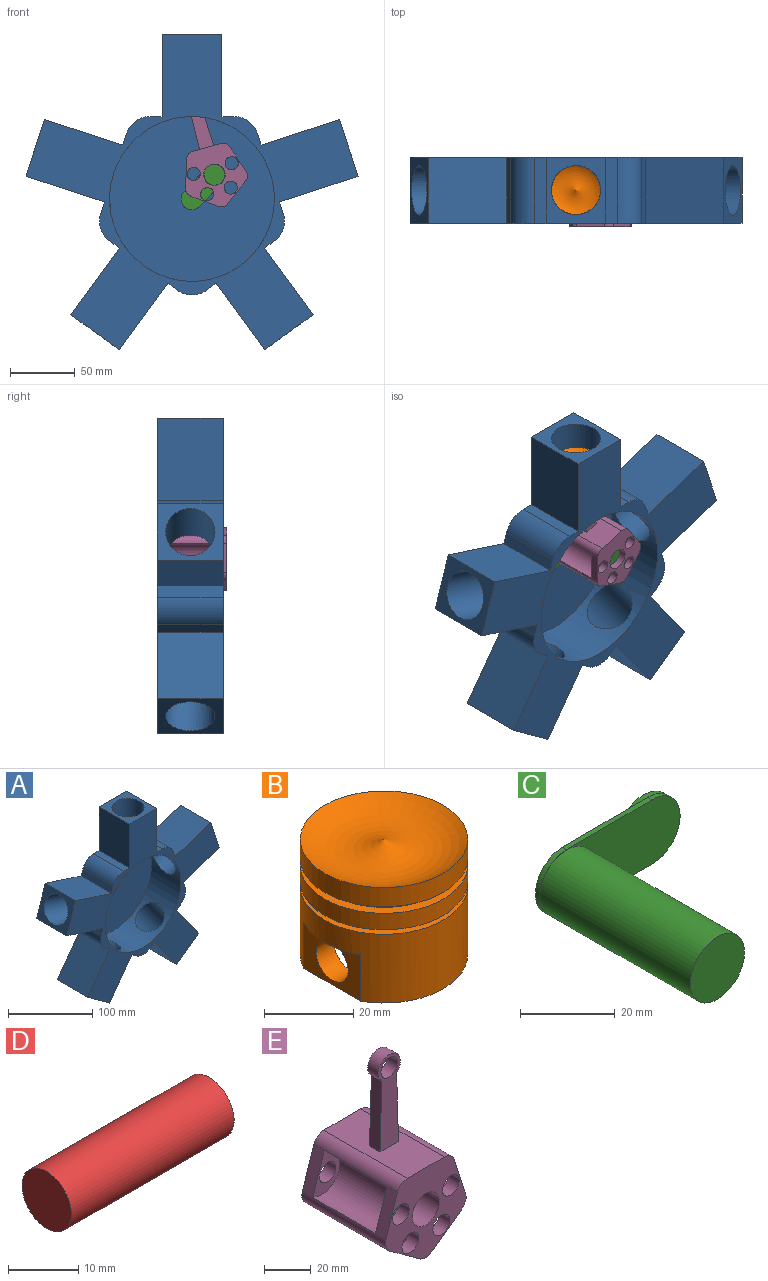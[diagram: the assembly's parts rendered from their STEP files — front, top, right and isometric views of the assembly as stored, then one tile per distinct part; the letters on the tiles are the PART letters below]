
ASSEMBLY  parts=5 mates=6
PART A: 40 faces, bbox 255.8x50.8x243.3 mm
  f0: plane 50.8x7.46mm, normal (0.59,0,-0.81), area 468.5mm2, adj f1,f25,f26,f39
  f1: plane 51.37x50.8mm, normal (-0.81,0,-0.59), area 3225.8mm2, adj f0,f2,f25,f26
  f2: plane 50.8x37.32mm, normal (0.59,0,-0.81), area 1203.1mm2, adj f1,f3,f25,f26,f34
  f3: plane 51.38x50.8mm, normal (0.81,0,0.59), area 3225.8mm2, adj f2,f4,f25,f26
  f4: plane 50.8x7.46mm, normal (0.59,0,-0.81), area 468.5mm2, adj f3,f25,f26,f35
  f5: plane 50.8x8.77mm, normal (0.95,0,0.31), area 468.5mm2, adj f6,f25,f26,f35
  f6: plane 60.39x50.8mm, normal (0.31,0,-0.95), area 3225.8mm2, adj f5,f7,f25,f26
  f7: plane 50.8x43.88mm, normal (0.95,0,0.31), area 1203.7mm2, adj f6,f8,f25,f26,f33
  f8: plane 60.39x50.8mm, normal (-0.31,0,0.95), area 3225.8mm2, adj f7,f9,f25,f26
  f9: plane 50.8x8.78mm, normal (0.95,0,0.31), area 468.8mm2, adj f8,f25,f26,f36
  f10: plane 50.8x9.22mm, normal (0,0,1), area 468.5mm2, adj f11,f25,f26,f36
  f11: plane 63.5x50.8mm, normal (1,0,0), area 3225.8mm2, adj f10,f12,f25,f26
  f12: plane 50.8x46.14mm, normal (0,0,1), area 1204mm2, adj f11,f13,f25,f26,f32
  f13: plane 63.5x50.8mm, normal (-1,0,0), area 3225.8mm2, adj f12,f14,f25,f26
  f14: plane 50.8x9.22mm, normal (0,0,1), area 468.5mm2, adj f13,f25,f26,f37
  f15: plane 50.8x8.77mm, normal (-0.95,0,0.31), area 468.5mm2, adj f16,f25,f26,f37
  f16: plane 60.39x50.8mm, normal (0.31,0,0.95), area 3225.8mm2, adj f15,f17,f25,f26
  f17: plane 50.8x43.87mm, normal (-0.95,0,0.31), area 1203.1mm2, adj f16,f18,f25,f26,f31
  f18: plane 60.39x50.8mm, normal (-0.31,0,-0.95), area 3225.8mm2, adj f17,f19,f25,f26
  f19: plane 50.8x8.77mm, normal (-0.95,0,0.31), area 468.5mm2, adj f18,f25,f26,f38
  f20: plane 50.8x7.46mm, normal (-0.59,0,-0.81), area 468.5mm2, adj f21,f25,f26,f38
  f21: plane 51.37x50.8mm, normal (-0.81,0,0.59), area 3225.8mm2, adj f20,f22,f25,f26
  f22: plane 50.8x37.33mm, normal (-0.59,0,-0.81), area 1204mm2, adj f21,f23,f25,f26,f30
  f23: plane 51.37x50.8mm, normal (0.81,0,-0.59), area 3225.8mm2, adj f22,f24,f25,f26
  f24: plane 50.8x7.46mm, normal (-0.59,0,-0.81), area 468.5mm2, adj f23,f25,f26,f39
  f25: plane 255.82x243.31mm, normal (0,-1,0), area 16451.4mm2, adj f0,f1,f2,f3,f4,f5,f6,f7
  f26: plane 255.82x243.31mm, normal (0,1,0), area 28901.7mm2, adj f0,f1,f2,f3,f4,f5,f6,f7
  f27: cylinder r=63.5mm len=127mm, axis (0,-1,0), area 13980.7mm2, adj f25,f28,f30,f31,f32,f33,f34
  f28: plane 127x127mm, normal (0,-1,0), area 12450.3mm2, adj f27,f29
  f29: cylinder r=8.32mm len=16.64mm, axis (0,1,0), area 66.4mm2, adj f26,f28
  f30: cylinder r=19.05mm len=76.13mm, axis (-0.59,0,-0.81), area 7774.4mm2, adj f22,f27
  f31: cylinder r=19.05mm len=74.95mm, axis (-0.95,0,0.31), area 7774.4mm2, adj f17,f27
  f32: cylinder r=19.05mm len=66.43mm, axis (0,0,1), area 7774.4mm2, adj f12,f27
  f33: cylinder r=19.05mm len=74.95mm, axis (0.95,0,0.31), area 7774.4mm2, adj f7,f27
  f34: cylinder r=19.05mm len=76.13mm, axis (0.59,0,-0.81), area 7774.4mm2, adj f2,f27
  f35: cylinder r=19.05mm len=50.8mm, axis (0,1,0), area 1216.1mm2, adj f4,f5,f25,f26
  f36: cylinder r=19.05mm len=50.8mm, axis (0,1,0), area 1216.1mm2, adj f9,f10,f25,f26
  f37: cylinder r=19.05mm len=50.8mm, axis (0,1,0), area 1216.1mm2, adj f14,f15,f25,f26
  f38: cylinder r=19.05mm len=50.8mm, axis (0,1,0), area 1216.1mm2, adj f19,f20,f25,f26
  f39: cylinder r=19.05mm len=50.8mm, axis (0,1,0), area 1216.1mm2, adj f0,f24,f25,f26
PART B: 22 faces, bbox 37.6x37.6x31.8 mm
  f0: plane 37.59x32.66mm, normal (0,0,-1), area 407.5mm2, adj f9,f13,f14,f15,f16,f17,f18
  f1: plane 18.1x2.32mm, normal (0,0,-1), area 28.4mm2, adj f9,f14
  f2: cylinder r=18.8mm len=37.59mm, axis (0,0,-1), area 532.7mm2, adj f3,f12
  f3: plane 37.59x37.59mm, normal (0,0,1), area 256.8mm2, adj f2,f4
  f4: cylinder r=16.48mm len=32.96mm, axis (0,0,-1), area 189.7mm2, adj f3,f5
  f5: plane 37.59x37.59mm, normal (0,0,-1), area 256.8mm2, adj f4,f6
  f6: cylinder r=18.8mm len=37.59mm, axis (0,0,-1), area 620mm2, adj f5,f7
  f7: torus R=9.4mm, axis (0,0,-1), area 1174.3mm2, adj f6
  f8: plane 19.13x2.62mm, normal (0,0,-1), area 33.8mm2, adj f9,f13
  f9: cylinder r=18.8mm len=37.59mm, axis (0,0,-1), area 1736mm2, adj f0,f1,f8,f10,f13,f14
  f10: plane 37.59x37.59mm, normal (0,0,1), area 409.8mm2, adj f9,f11
  f11: cylinder r=14.93mm len=29.86mm, axis (0,0,-1), area 119mm2, adj f10,f12
  f12: plane 37.59x37.59mm, normal (0,0,-1), area 409.8mm2, adj f2,f11
  f13: plane 19.13x12.7mm, normal (1,0,0), area 161.9mm2, adj f0,f8,f9,f21
  f14: plane 18.1x12.7mm, normal (-1,0,0), area 148.7mm2, adj f0,f1,f9,f20
  f15: plane 22.8x17.78mm, normal (-1,0,0), area 324.3mm2, adj f0,f16,f18,f19,f21
  f16: cylinder r=14.68mm len=21.6mm, axis (0,0,-1), area 431.6mm2, adj f0,f15,f17,f19
  f17: plane 22.8x17.78mm, normal (1,0,0), area 324.3mm2, adj f0,f16,f18,f19,f20
  f18: cylinder r=13.96mm len=21.6mm, axis (0,0,-1), area 439.2mm2, adj f0,f15,f17,f19
  f19: plane 32.66x21.6mm, normal (0,0,-1), area 640.2mm2, adj f15,f16,f17,f18
  f20: cylinder r=5.08mm len=10.16mm, axis (1,0,0), area 179.7mm2, adj f14,f17
  f21: cylinder r=5.08mm len=10.16mm, axis (1,0,0), area 173.1mm2, adj f13,f15
PART C: 12 faces, bbox 41.9x47.5x16.6 mm
  f0: cylinder r=8.31mm len=16.61mm, axis (0,1,0), area 66.3mm2, adj f1,f2,f5,f8
  f1: plane 16.61x16.61mm, normal (0,1,0), area 216.7mm2, adj f0
  f2: plane 33.47x16.61mm, normal (0,1,0), area 412.8mm2, adj f0,f3,f5,f6
  f3: plane 25.4x1.27mm, normal (-0.01,0,-1), area 32.3mm2, adj f2,f4,f6,f7,f8
  f4: cylinder r=8.31mm len=16.61mm, axis (0,1,0), area 33.3mm2, adj f3,f5,f7,f8
  f5: plane 25.46x1.27mm, normal (-0.01,0,1), area 32.3mm2, adj f0,f2,f4,f6,f7
  f6: cylinder r=8.13mm len=16.26mm, axis (0,1,0), area 32.4mm2, adj f2,f3,f5,f7,f9
  f7: plane 39.82x16.61mm, normal (0,-1,0), area 425.3mm2, adj f3,f4,f5,f6,f10
  f8: plane 16.61x8.42mm, normal (0,1,0), area 1mm2, adj f0,f3,f4
  f9: plane 10.84x2.09mm, normal (0,1,0), area 0.1mm2, adj f6,f10
  f10: cylinder r=8.09mm len=44.96mm, axis (0,1,0), area 2284.1mm2, adj f7,f9,f11
  f11: plane 16.17x16.17mm, normal (0,-1,0), area 205.4mm2, adj f10
PART D: 3 faces, bbox 32.7x9.9x9.9 mm
  f0: cylinder r=4.95mm len=32.66mm, axis (-1,0,0), area 1016.5mm2, adj f1,f2
  f1: plane 9.91x9.91mm, normal (1,0,0), area 77.1mm2, adj f0
  f2: plane 9.91x9.91mm, normal (-1,0,0), area 77.1mm2, adj f0
PART E: 43 faces, bbox 49.1x50.8x95.7 mm
  f0: plane 48.46x13.55mm, normal (0,-1,0), area 422.5mm2, adj f11,f25,f26,f27,f28
  f1: plane 21.51x19.42mm, normal (0,-1,0), area 162.5mm2, adj f5,f18,f21
  f2: plane 22.6x16.5mm, normal (0,-1,0), area 161.6mm2, adj f13,f15,f24
  f3: plane 22.61x16.54mm, normal (0,-1,0), area 162.6mm2, adj f9,f16,f23
  f4: plane 21.51x19.42mm, normal (0,-1,0), area 162.6mm2, adj f7,f17,f22
  f5: plane 18.18x13.21mm, normal (-0.59,0,-0.81), area 142.7mm2, adj f1,f6,f19,f20
  f6: cylinder r=6.35mm len=50.8mm, axis (0,1,0), area 405.4mm2, adj f5,f7,f20,f21,f22,f34,f35,f37
  f7: plane 18.18x13.21mm, normal (0.59,0,-0.81), area 142.7mm2, adj f4,f6,f8,f20
  f8: cylinder r=6.35mm len=50.8mm, axis (0,1,0), area 405.4mm2, adj f7,f9,f20,f22,f23,f35,f36,f37
  f9: plane 21.37x6.95mm, normal (0.95,0,0.31), area 142.7mm2, adj f3,f8,f10,f20
  f10: cylinder r=6.35mm len=50.8mm, axis (0,1,0), area 405.4mm2, adj f9,f11,f20,f23,f36,f37
  f11: plane 50.8x22.47mm, normal (0,0,1), area 1070.3mm2, adj f0,f10,f12,f20,f25,f27,f29,f37
  f12: cylinder r=6.35mm len=50.8mm, axis (0,1,0), area 405.4mm2, adj f11,f13,f20,f24,f33,f37
  f13: plane 21.37x6.95mm, normal (-0.95,0,0.31), area 142.7mm2, adj f2,f12,f19,f20
  f14: cylinder r=8.26mm len=50.8mm, axis (0,1,0), area 2634.9mm2, adj f20,f37
  f15: cylinder r=5.08mm len=10.16mm, axis (0,1,0), area 202.7mm2, adj f2,f20
  f16: cylinder r=5.08mm len=10.16mm, axis (0,1,0), area 202.7mm2, adj f3,f20
  f17: cylinder r=5.08mm len=10.16mm, axis (0,1,0), area 202.7mm2, adj f4,f20
  f18: cylinder r=5.08mm len=10.16mm, axis (0,1,0), area 202.7mm2, adj f1,f20
  f19: cylinder r=6.35mm len=50.8mm, axis (0,1,0), area 405.4mm2, adj f5,f13,f20,f21,f24,f33,f34,f37
  f20: plane 49.06x47.28mm, normal (0,1,0), area 1170.9mm2, adj f5,f6,f7,f8,f9,f10,f11,f12
  f21: cylinder r=11.38mm len=38.1mm, axis (0,1,0), area 1497.6mm2, adj f1,f6,f19,f31
  f22: cylinder r=11.38mm len=38.1mm, axis (0,1,0), area 1497.9mm2, adj f4,f6,f8,f32
  f23: cylinder r=11.38mm len=38.1mm, axis (0,1,0), area 1498mm2, adj f3,f8,f10,f38
  f24: cylinder r=11.37mm len=38.1mm, axis (0,1,0), area 1494.6mm2, adj f2,f12,f19,f30
  f25: plane 36.6x6.35mm, normal (1,0,0.03), area 232.5mm2, adj f0,f11,f26,f29
  f26: cylinder r=6.77mm len=13.55mm, axis (0,1,0), area 208.1mm2, adj f0,f25,f27,f29
  f27: plane 36.6x6.35mm, normal (-1,0,0.03), area 232.5mm2, adj f0,f11,f26,f29
  f28: cylinder r=5.08mm len=10.16mm, axis (0,1,0), area 202.7mm2, adj f0,f29
  f29: plane 48.46x13.55mm, normal (0,1,0), area 422.5mm2, adj f11,f25,f26,f27,f28
  f30: plane 22.6x16.5mm, normal (0,1,0), area 161.6mm2, adj f24,f33,f42
  f31: plane 21.51x19.42mm, normal (0,1,0), area 162.5mm2, adj f21,f34,f41
  f32: plane 21.51x19.42mm, normal (0,1,0), area 162.6mm2, adj f22,f35,f40
  f33: plane 21.37x6.95mm, normal (-0.95,0,0.31), area 142.7mm2, adj f12,f19,f30,f37
  f34: plane 18.18x13.21mm, normal (-0.59,0,-0.81), area 142.7mm2, adj f6,f19,f31,f37
  f35: plane 18.18x13.21mm, normal (0.59,0,-0.81), area 142.7mm2, adj f6,f8,f32,f37
  f36: plane 21.37x6.95mm, normal (0.95,0,0.31), area 142.7mm2, adj f8,f10,f37,f38
  f37: plane 49.06x47.28mm, normal (0,-1,0), area 1170.9mm2, adj f6,f8,f10,f11,f12,f14,f19,f33
  f38: plane 22.61x16.54mm, normal (0,1,0), area 162.6mm2, adj f23,f36,f39
  f39: cylinder r=5.08mm len=10.16mm, axis (0,-1,0), area 202.7mm2, adj f37,f38
  f40: cylinder r=5.08mm len=10.16mm, axis (0,-1,0), area 202.7mm2, adj f32,f37
  f41: cylinder r=5.08mm len=10.16mm, axis (0,-1,0), area 202.7mm2, adj f31,f37
  f42: cylinder r=5.08mm len=10.16mm, axis (0,-1,0), area 202.7mm2, adj f30,f37
PLACE A t=(-273.89,22.57,107.13)mm fixed
PLACE B rot(axis=(0,0,1),90deg) t=(-273.89,-2.83,193.2)mm
PLACE C rot(axis=(0,1,0),132.9deg) t=(-273.89,22.57,107.13)mm
PLACE D rot(axis=(0,0,1),90deg) t=(-273.89,-19.31,186.85)mm
PLACE E rot(axis=(0.14,0,-0.99),180deg) t=(-273.42,-30.77,124.93)mm
MATE cylindrical B.f2 <-> A.f32  axis (0,0,-1) through (-273.89,-2.83,212.25)mm
MATE slider D.f0 <-> B.f20  axis (0,1,0) through (-273.89,13.35,186.85)mm
MATE revolute C.f0 <-> A.f27  axis (0,1,0) through (-273.89,22.57,107.13)mm
MATE cylindrical D.f0 <-> E.f26  axis (0,-1,0) through (-273.89,-2.98,186.85)mm
MATE planar D.f0 <-> B.f20  axis (0,1,0) through (-273.89,13.35,186.85)mm
MATE revolute E.f14 <-> C.f6  axis (0,-1,0) through (-256.61,20.03,125.74)mm
